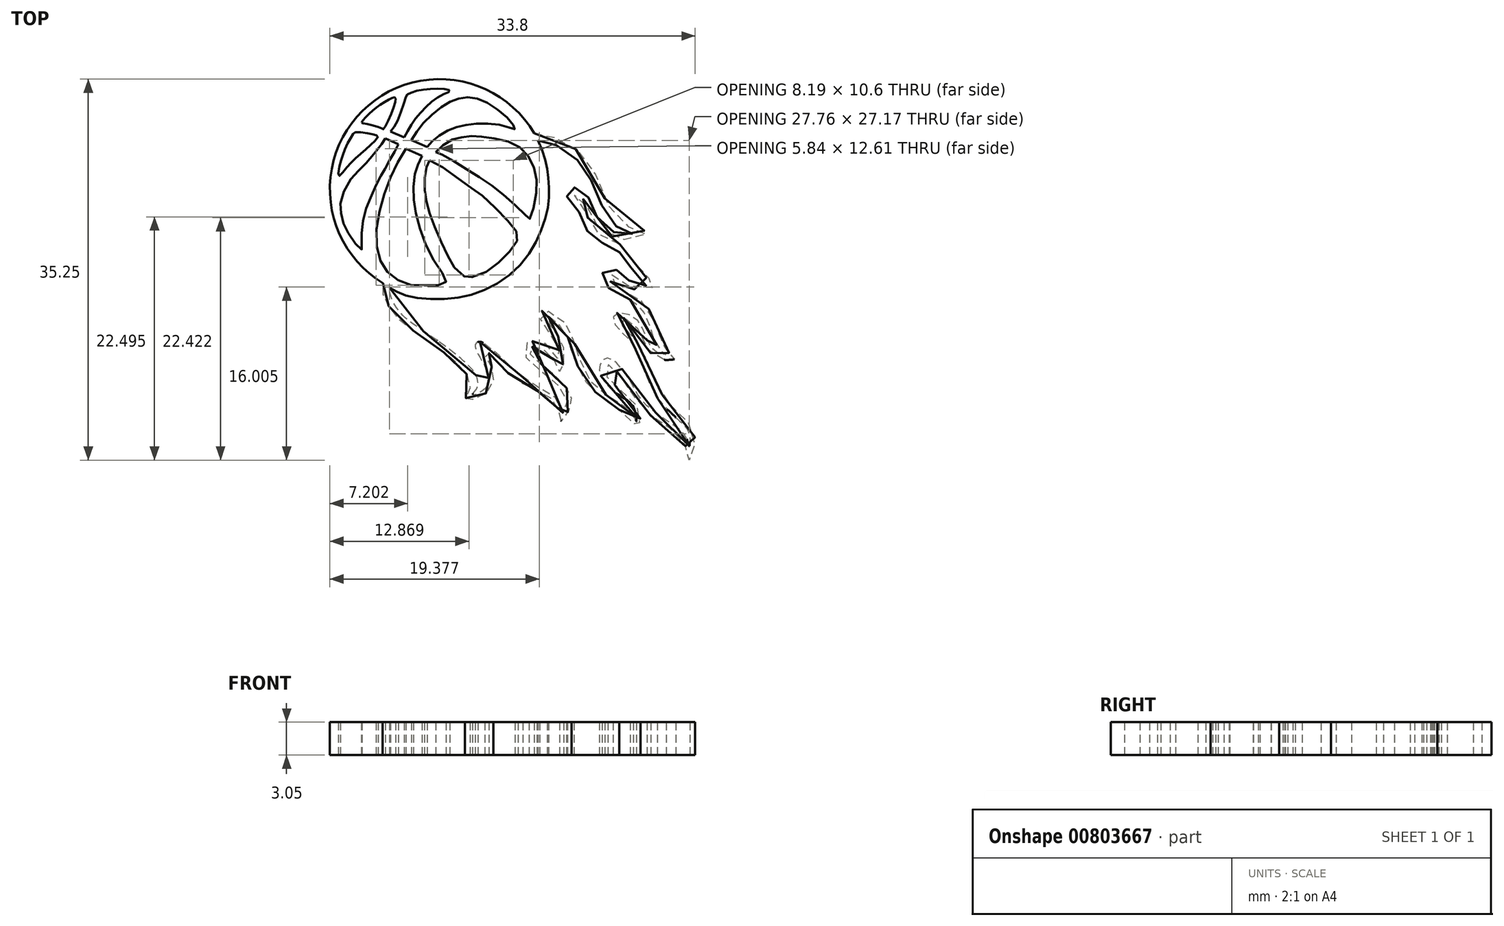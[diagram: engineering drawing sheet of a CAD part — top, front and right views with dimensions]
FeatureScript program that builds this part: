
annotation { "Feature Type Name" : "Feature", "Feature Type Description" : "" }
export const myFeature = defineFeature(function(context is Context, id is Id, definition is map)
    precondition{}
    {
        {
            var Q0;
            Q0=qCreatedBy(makeId("Top.planeOp"),FACE);
            var sketch = newSketch(context, id + "F0", { "sketchPlane" : qUnion([Q0])});
            skFitSpline(sketch, "E0", {"points": [v(-13.3, 12.08) * mm, v(-12.76, 12.76) * mm, v(-11.66, 13.68) * mm, v(-10.52, 14.35) * mm, v(-10.21, 14.4) * mm, v(-10.32, 13.51) * mm, v(-11.3, 11.48) * mm, v(-11.44, 11.55) * mm, v(-13.05, 12) * mm, v(-13.3, 12.08) * mm]});
            skFitSpline(sketch, "E1", {"points": [v(-10.63, 11.26) * mm, v(-9.86, 12.55) * mm, v(-9.2, 14.55) * mm, v(-9.08, 14.7) * mm, v(-8.32, 15) * mm, v(-6.92, 15.2) * mm, v(-5.42, 15.17) * mm, v(-5.15, 15) * mm, v(-5.87, 14.64) * mm, v(-7.23, 13.66) * mm, v(-8.49, 12.2) * mm, v(-9.37, 10.7) * mm], "startDerivative": vector(7.7, 10.26) * mm, "endDerivative": vector(-7.34, -13.64) * mm});
            skFitSpline(sketch, "E2", {"points": [v(-8.7, 10.48) * mm, v(-7.61, 12) * mm, v(-5.8, 13.63) * mm, v(-4.3, 14.32) * mm, v(-2.86, 14.38) * mm, v(-0.84, 13.4) * mm, v(0.74, 11.87) * mm, v(0.87, 11.48) * mm, v(0.45, 11.61) * mm, v(-1.45, 12) * mm, v(-3.55, 11.87) * mm, v(-5.07, 11.48) * mm, v(-6.49, 10.61) * mm, v(-7.23, 9.84) * mm], "startDerivative": vector(11.23, 17.7) * mm, "endDerivative": vector(-10.12, -11.98) * mm});
            skFitSpline(sketch, "E3", {"points": [v(-6.43, 9.36) * mm, v(-5.33, 10.3) * mm, v(-4.35, 10.68) * mm, v(-3.1, 10.84) * mm, v(-1.75, 10.73) * mm, v(0.64, 10.19) * mm, v(2.05, 9.08) * mm, v(2.83, 7.2) * mm, v(2.78, 4.95) * mm, v(2.24, 3.16) * mm, v(2.07, 3.27) * mm, v(0.4, 4.93) * mm, v(-1.83, 6.66) * mm, v(-4.2, 8.15) * mm, v(-6.12, 9.24) * mm, v(-6.43, 9.36) * mm]});
            skFitSpline(sketch, "E4", {"points": [v(-7.03, 8.58) * mm, v(-7.19, 8.3) * mm, v(-7.38, 7.7) * mm, v(-7.48, 6.66) * mm, v(-7.43, 5.53) * mm, v(-7.24, 4.53) * mm, v(-6.9, 3.34) * mm, v(-6.17, 1.54) * mm, v(-5.37, -0.17) * mm, v(-4.67, -1.35) * mm, v(-3.7, -2.2) * mm, v(-3.37, -2.27) * mm, v(-1.95, -1.81) * mm, v(-0.47, -0.72) * mm, v(0.76, 0.58) * mm, v(1.17, 1.47) * mm, v(0.9, 2.2) * mm, v(-0.36, 3.62) * mm, v(-2.16, 5.33) * mm, v(-3.37, 6.2) * mm, v(-5.17, 7.5) * mm, v(-7.03, 8.58) * mm]});
            skFitSpline(sketch, "E5", {"points": [v(-7.7, 9) * mm, v(-8.08, 8.19) * mm, v(-8.4, 7.24) * mm, v(-8.5, 5.58) * mm, v(-8.32, 3.95) * mm, v(-7.64, 1.5) * mm, v(-6.37, -1.06) * mm, v(-5.5, -2.44) * mm, v(-5.65, -2.84) * mm, v(-7.1, -2.95) * mm, v(-8.9, -2.9) * mm, v(-10.5, -2.08) * mm, v(-11.51, -0.83) * mm, v(-11.97, 1.44) * mm, v(-11.48, 4.56) * mm, v(-10.45, 7.44) * mm, v(-9.2, 9.66) * mm], "startDerivative": vector(-8.83, -18.37) * mm, "endDerivative": vector(17.62, 28.82) * mm});
            skFitSpline(sketch, "E6", {"points": [v(-9.92, 10.1) * mm, v(-10.28, 9.35) * mm, v(-10.87, 8.32) * mm, v(-11.3, 7.5) * mm, v(-11.7, 6.84) * mm, v(-12.52, 5.07) * mm, v(-13.05, 3.64) * mm, v(-13.3, 1.78) * mm, v(-13.3, 1.2) * mm, v(-13.3, 0.33) * mm, v(-14.07, 1.17) * mm, v(-14.88, 2.52) * mm, v(-15.22, 3.72) * mm, v(-15.22, 4.86) * mm, v(-14.36, 6.8) * mm, v(-13.3, 7.9) * mm, v(-12.36, 8.95) * mm, v(-11.3, 10.28) * mm, v(-11.1, 10.63) * mm], "startDerivative": vector(-7.16, -15.6) * mm, "endDerivative": vector(4.84, 8.94) * mm});
            skLineSegment(sketch, "E7", {"start": v(-10.63, 11.26) * mm, "end": v(-9.37, 10.7) * mm});
            skLineSegment(sketch, "E8", {"start": v(-8.7, 10.48) * mm, "end": v(-7.23, 9.84) * mm});
            skLineSegment(sketch, "E9", {"start": v(-9.2, 9.66) * mm, "end": v(-7.7, 9) * mm});
            skLineSegment(sketch, "E10", {"start": v(-11.1, 10.63) * mm, "end": v(-9.92, 10.1) * mm});
            skArc(sketch, "E11", {"start": v(2.68, 11.1) * mm, "mid": v(-13.23, 13.17) * mm, "end": v(-11.32, -2.76) * mm});
            skPoint(sketch, "E11.first.point", {"position": v(4, 4.75) * mm});
            skPoint(sketch, "E11.second.point", {"position": v(-16.05, 7.9) * mm});
            skPoint(sketch, "E11.third.point", {"position": v(-12.7, -1.76) * mm});
            skFitSpline(sketch, "E12", {"points": [v(-13.91, 11.2) * mm, v(-14.1, 11.04) * mm, v(-14.51, 10.33) * mm, v(-15.03, 9.17) * mm, v(-15.32, 8.13) * mm, v(-15.42, 7.15) * mm, v(-14.94, 7.64) * mm, v(-14.14, 8.52) * mm, v(-13.08, 9.46) * mm, v(-12.14, 10.33) * mm, v(-11.79, 10.82) * mm, v(-12.05, 10.96) * mm, v(-12.72, 11.1) * mm, v(-13.91, 11.2) * mm]});
            skFitSpline(sketch, "E13", {"points": [v(3.03, 10.45) * mm, v(3.97, 10.27) * mm, v(5.64, 9.47) * mm, v(7.23, 8.01) * mm, v(8.17, 6.26) * mm, v(9.15, 3.98) * mm, v(10.47, 2.38) * mm, v(11.84, 1.86) * mm, v(11.18, 1.74) * mm, v(9.97, 1.97) * mm, v(8.65, 3.09) * mm, v(7.96, 4.6) * mm, v(7.37, 5.6) * mm, v(6.52, 6.07) * mm, v(5.84, 5.96) * mm, v(5.66, 5.35) * mm, v(6.32, 4.5) * mm, v(7.14, 3.22) * mm, v(7.62, 2) * mm, v(8.44, 1.22) * mm, v(9.79, 0.62) * mm, v(10.68, 0) * mm, v(11.3, -0.77) * mm, v(12.11, -2.09) * mm, v(12.8, -2.64) * mm, v(13.46, -2.77) * mm, v(13.05, -2.98) * mm, v(12.14, -2.91) * mm, v(11.06, -2.23) * mm, v(10.52, -1.68) * mm, v(9.7, -1.4) * mm, v(9.06, -1.72) * mm, v(9.01, -2.48) * mm, v(9.74, -3.37) * mm, v(11.56, -4.3) * mm], "startDerivative": vector(33.75, -3.92) * mm, "endDerivative": vector(52.28, -22.72) * mm});
            skPoint(sketch, "E14", {"position": v(-11.32, -2.76) * mm});
            skPoint(sketch, "E15", {"position": v(2.68, 11.1) * mm});
            skFitSpline(sketch, "E16", {"points": [v(11.56, -4.3) * mm, v(12.13, -4.72) * mm, v(12.89, -5.56) * mm, v(13.64, -7.62) * mm, v(14.44, -9.05) * mm, v(14.9, -9.37) * mm, v(14.5, -9.4) * mm, v(13.89, -9.12) * mm, v(13.3, -8.37) * mm, v(12.73, -7) * mm, v(12.34, -6.32) * mm, v(11.56, -5.75) * mm, v(10.5, -5.5) * mm, v(10.03, -5.8) * mm, v(10.03, -6.39) * mm, v(10.7, -7.23) * mm, v(11.56, -8.07) * mm, v(12.16, -9.05) * mm, v(12.89, -10.92) * mm, v(13.6, -12.52) * mm, v(14.55, -13.98) * mm, v(16.49, -15.87) * mm, v(17.06, -16.94) * mm, v(17.01, -17.86) * mm, v(16.83, -17.29) * mm, v(16.3, -16.49) * mm, v(14.73, -15.35) * mm, v(13.4, -14.37) * mm, v(12.5, -13.46) * mm, v(11.56, -11.81) * mm, v(10.63, -10.51) * mm, v(10.01, -9.92) * mm, v(9.33, -9.72) * mm, v(8.85, -10.13) * mm, v(8.76, -11.1) * mm, v(9.42, -12.18) * mm, v(10.74, -13.27) * mm, v(11.88, -14.3) * mm, v(12.13, -15.55) * mm, v(11.8, -14.73) * mm, v(10.95, -14.14) * mm, v(9.76, -13.39) * mm, v(8.32, -12.36) * mm, v(7.37, -10.92) * mm, v(6.52, -8.76) * mm, v(6.07, -7.39) * mm, v(5.52, -6.45) * mm, v(4.26, -5.5) * mm, v(3.3, -5.38) * mm, v(3.3, -6.27) * mm, v(4.22, -7.64) * mm, v(4.74, -8.44) * mm, v(5, -9.08) * mm, v(4.93, -9.94) * mm, v(4.68, -9.28) * mm, v(3.63, -8.32) * mm, v(2.3, -8.16) * mm, v(1.64, -8.73) * mm, v(2.03, -9.8) * mm, v(3.3, -10.9) * mm, v(4.68, -12.02) * mm, v(5.5, -12.98) * mm, v(5.72, -14.1) * mm, v(5.36, -14.82) * mm, v(5.27, -14.23) * mm, v(4.47, -13.23) * mm, v(2.94, -12.34) * mm, v(1.03, -11.02) * mm, v(-0.41, -9.62) * mm, v(-1.71, -8.5) * mm, v(-2.4, -8.19) * mm, v(-2.76, -8.4) * mm, v(-2.65, -9.05) * mm, v(-2.05, -10.15) * mm, v(-1.62, -11.13) * mm, v(-1.8, -12.45) * mm, v(-3.03, -13.11) * mm, v(-2.62, -12.48) * mm, v(-2.65, -11.47) * mm, v(-3.28, -10.51) * mm, v(-5.52, -8.64) * mm, v(-7.85, -7.02) * mm, v(-9.44, -5.8) * mm, v(-10.5, -4.3) * mm, v(-10.74, -3.2) * mm], "startDerivative": vector(61.22, -43.14) * mm, "endDerivative": vector(-11.6, 94) * mm});
            skFitSpline(sketch, "E17", {"points": [v(3.03, 10.45) * mm, v(3.76, 8.45) * mm, v(3.98, 6.72) * mm, v(4, 4.75) * mm, v(3.32, 2.16) * mm, v(1.43, -1.04) * mm, v(-2.17, -3.5) * mm, v(-5.82, -4.23) * mm, v(-9.2, -3.91) * mm, v(-10.74, -3.2) * mm], "startDerivative": vector(8.75, -20.74) * mm, "endDerivative": vector(-15.51, 9.13) * mm});
            skFitSpline(sketch, "E18", {"points": [v(2.68, 11.1) * mm, v(3.51, 11) * mm, v(4.52, 10.74) * mm, v(5.75, 10.17) * mm, v(6.9, 9.32) * mm, v(7.92, 8.14) * mm, v(8.85, 6.01) * mm, v(9.73, 4.07) * mm, v(10.9, 2.8) * mm, v(12.06, 2.21) * mm, v(13.14, 1.97) * mm, v(12.69, 1.6) * mm, v(11.87, 1.31) * mm, v(10.57, 1.32) * mm, v(9.1, 1.96) * mm, v(8.2, 2.84) * mm, v(7.62, 4.15) * mm, v(7.07, 5.16) * mm, v(6.54, 5.47) * mm, v(6.4, 5.35) * mm, v(6.78, 4.7) * mm, v(7.36, 3.95) * mm, v(7.89, 2.62) * mm, v(8.52, 1.85) * mm, v(9.43, 1.33) * mm, v(10.36, 0.97) * mm, v(11.46, 0) * mm, v(12.03, -0.98) * mm, v(12.4, -1.6) * mm, v(12.97, -2.23) * mm, v(14.07, -2.4) * mm, v(13.94, -2.72) * mm, v(13.49, -3.3) * mm, v(12.53, -3.53) * mm, v(10.9, -2.68) * mm, v(10.55, -2.3) * mm, v(9.88, -2.01) * mm, v(9.56, -2.08) * mm, v(9.68, -2.55) * mm, v(10.28, -3.1) * mm, v(11.8, -3.9) * mm, v(12.9, -4.69) * mm, v(13.47, -5.56) * mm, v(14.03, -7.07) * mm, v(14.66, -8.53) * mm, v(15.16, -9.25) * mm, v(15.83, -9.75) * mm, v(15.4, -9.84) * mm, v(14.75, -9.87) * mm, v(13.84, -9.54) * mm, v(13.09, -8.72) * mm, v(12.36, -7.17) * mm, v(11.88, -6.49) * mm, v(11, -6) * mm, v(10.57, -5.97) * mm, v(10.56, -6.34) * mm, v(11.12, -7) * mm, v(11.9, -7.82) * mm, v(12.46, -8.68) * mm, v(13.3, -10.41) * mm, v(13.98, -12.15) * mm, v(15.01, -13.76) * mm, v(16.16, -14.85) * mm, v(17.36, -16.33) * mm, v(17.53, -17.69) * mm, v(17.2, -18.8) * mm, v(17.04, -19.14) * mm, v(16.93, -18.79) * mm, v(16.7, -17.88) * mm, v(15.96, -16.79) * mm, v(14.97, -16) * mm, v(14.03, -15.4) * mm, v(12.73, -14.36) * mm, v(11.79, -12.95) * mm, v(10.66, -11.4) * mm, v(9.87, -10.43) * mm, v(9.42, -10.3) * mm, v(9.25, -10.56) * mm, v(9.37, -11.37) * mm, v(10.13, -12.19) * mm, v(10.98, -12.94) * mm, v(11.91, -13.78) * mm, v(12.48, -14.85) * mm, v(12.46, -15.55) * mm, v(12.18, -16.4) * mm, v(12, -15.98) * mm, v(11.74, -15.51) * mm, v(10.54, -14.5) * mm], "startDerivative": vector(79.85, -6.59) * mm, "endDerivative": vector(-102.26, 79.5) * mm});
            skFitSpline(sketch, "E19", {"points": [v(10.54, -14.5) * mm, v(9.79, -14) * mm, v(8.24, -12.77) * mm, v(7.46, -11.87) * mm, v(6.45, -9.88) * mm, v(5.9, -8.25) * mm, v(5.6, -7.4) * mm, v(4.36, -6.06) * mm, v(3.95, -5.9) * mm, v(4.02, -6.4) * mm, v(4.73, -7.49) * mm, v(5.3, -8.43) * mm, v(5.4, -9.89) * mm, v(5.09, -11.03) * mm, v(4.9, -10.6) * mm, v(4.15, -9.43) * mm, v(3.06, -8.7) * mm, v(2.43, -8.7) * mm, v(2.23, -9.17) * mm, v(2.78, -9.84) * mm, v(4.46, -11.19) * mm, v(5.7, -12.54) * mm, v(6.12, -13.43) * mm, v(5.96, -14.34) * mm, v(5.21, -15.51) * mm, v(5.07, -15.1) * mm, v(4.63, -13.9) * mm, v(3.86, -13.18) * mm, v(2.22, -12.4) * mm, v(0.59, -11.35) * mm, v(-0.5, -10.32) * mm, v(-1.32, -9.39) * mm, v(-1.8, -9.16) * mm, v(-1.83, -9.6) * mm, v(-1.36, -10.36) * mm, v(-1.1, -11.54) * mm, v(-1.63, -12.81) * mm, v(-3.09, -13.55) * mm, v(-3.72, -13.56) * mm, v(-3.5, -13.25) * mm, v(-3.22, -12.2) * mm, v(-3.68, -11.05) * mm, v(-4.83, -9.88) * mm, v(-6.3, -8.72) * mm, v(-8.33, -7.3) * mm, v(-10, -5.96) * mm, v(-11, -4.5) * mm, v(-11.32, -3.64) * mm, v(-11.32, -2.76) * mm], "startDerivative": vector(-36.28, 22.9) * mm, "endDerivative": vector(3.68, 50.31) * mm});
            skSolve(sketch);
        }
        {
            var Q0;
            Q0=makeQuery(id+"F0.imprint","IMPRINT",FACE,{"disambiguationData":[TD([[makeQuery(id+"F0.imprint","IMPRINT",EDGE,{"derivedFrom":sQuery(id+"F0.wireOp",EDGE,"E0")}),1.0]])]});
            extrude(context, id + "F1", {"entities" : qUnion([Q0]), "depth" : 3.05 * mm, "offsetDistance" : 25.4 * mm});
        }
    });
